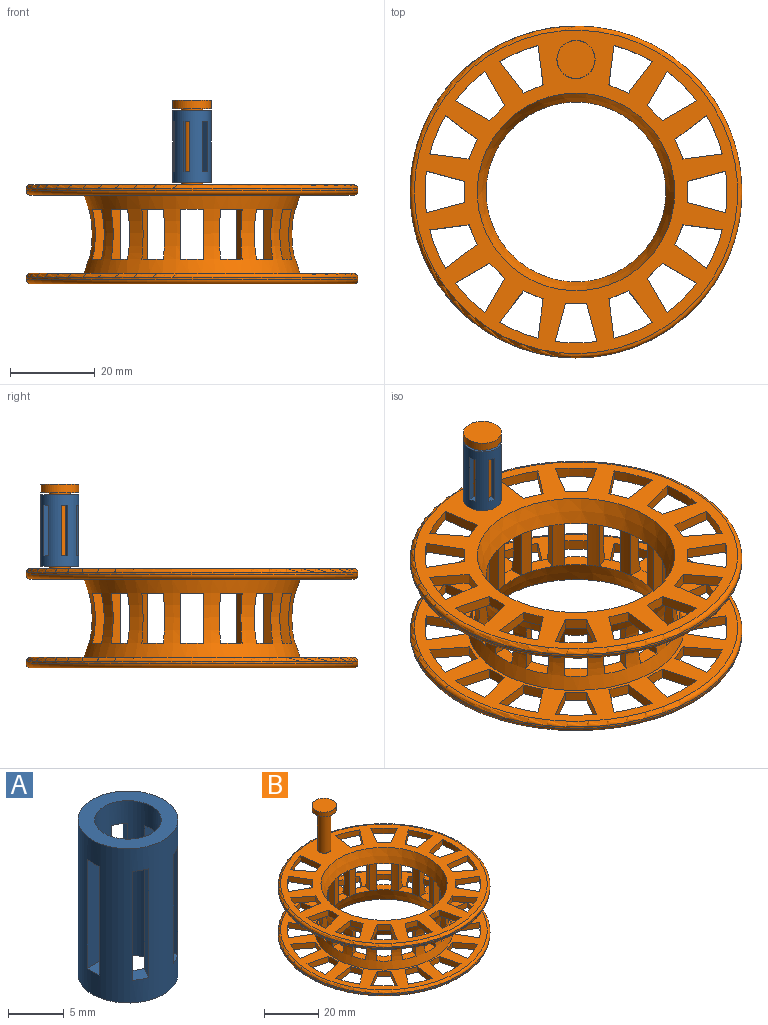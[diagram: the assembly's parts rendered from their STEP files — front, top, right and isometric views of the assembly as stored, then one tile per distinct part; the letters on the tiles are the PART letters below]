
ASSEMBLY  parts=2 mates=1
PART A: 28 faces, bbox 9x9x17 mm
  f0: cylinder r=4.5mm len=17mm, axis (0,0,1), area 372.2mm2, adj f2,f3,f4,f5,f6,f7,f8,f9
  f1: cylinder r=3mm len=17mm, axis (0,0,1), area 211.3mm2, adj f2,f3,f4,f5,f6,f7,f8,f9
  f2: plane 9x9mm, normal (0,0,1), area 35.3mm2, adj f0,f1
  f3: plane 9x9mm, normal (0,0,-1), area 35.3mm2, adj f0,f1
  f4: plane 12x1.33mm, normal (-0.87,0.5,0), area 18.4mm2, adj f0,f1,f6,f7
  f5: plane 12x1.33mm, normal (0.87,-0.5,0), area 18.4mm2, adj f0,f1,f6,f7
  f6: plane 2.08x2.07mm, normal (0,0,1), area 2.3mm2, adj f0,f1,f4,f5
  f7: plane 2.08x2.07mm, normal (0,0,-1), area 2.3mm2, adj f0,f1,f4,f5
  f8: plane 12x1.33mm, normal (-0.87,-0.5,0), area 18.4mm2, adj f0,f1,f10,f11
  f9: plane 12x1.33mm, normal (0.87,0.5,0), area 18.4mm2, adj f0,f1,f10,f11
  f10: plane 2.08x2.07mm, normal (0,0,1), area 2.3mm2, adj f0,f1,f8,f9
  f11: plane 2.08x2.07mm, normal (0,0,-1), area 2.3mm2, adj f0,f1,f8,f9
  f12: plane 12x1.53mm, normal (0,-1,0), area 18.4mm2, adj f0,f1,f14,f15
  f13: plane 12x1.53mm, normal (0,1,0), area 18.4mm2, adj f0,f1,f14,f15
  f14: plane 1.6x1.5mm, normal (0,0,1), area 2.3mm2, adj f0,f1,f12,f13
  f15: plane 1.6x1.5mm, normal (0,0,-1), area 2.3mm2, adj f0,f1,f12,f13
  f16: plane 12x1.33mm, normal (0.87,-0.5,0), area 18.4mm2, adj f0,f1,f18,f19
  f17: plane 12x1.33mm, normal (-0.87,0.5,0), area 18.4mm2, adj f0,f1,f18,f19
  f18: plane 2.08x2.07mm, normal (0,0,1), area 2.3mm2, adj f0,f1,f16,f17
  f19: plane 2.08x2.07mm, normal (0,0,-1), area 2.3mm2, adj f0,f1,f16,f17
  f20: plane 12x1.33mm, normal (0.87,0.5,0), area 18.4mm2, adj f0,f1,f22,f23
  f21: plane 12x1.33mm, normal (-0.87,-0.5,0), area 18.4mm2, adj f0,f1,f22,f23
  f22: plane 2.08x2.07mm, normal (0,0,1), area 2.3mm2, adj f0,f1,f20,f21
  f23: plane 2.08x2.07mm, normal (0,0,-1), area 2.3mm2, adj f0,f1,f20,f21
  f24: plane 12x1.53mm, normal (0,-1,0), area 18.4mm2, adj f0,f1,f25,f27
  f25: plane 1.6x1.5mm, normal (0,0,-1), area 2.3mm2, adj f0,f1,f24,f26
  f26: plane 12x1.53mm, normal (0,1,0), area 18.4mm2, adj f0,f1,f25,f27
  f27: plane 1.6x1.5mm, normal (0,0,1), area 2.3mm2, adj f0,f1,f24,f26
PART B: 221 faces, bbox 85x85x48.8 mm
  f0: cylinder r=21.25mm len=11.92mm, axis (0,0,1), area 33.7mm2, adj f20,f22,f203,f212
  f1: cylinder r=21.25mm len=11.92mm, axis (0,0,1), area 33.7mm2, adj f20,f22,f208,f211
  f2: cylinder r=21.25mm len=11.92mm, axis (0,0,1), area 33.7mm2, adj f20,f22,f151,f204
  f3: cylinder r=21.25mm len=11.92mm, axis (0,0,1), area 33.7mm2, adj f20,f22,f191,f200
  f4: cylinder r=21.25mm len=11.92mm, axis (0,0,1), area 33.7mm2, adj f20,f22,f196,f199
  f5: cylinder r=21.25mm len=11.92mm, axis (0,0,1), area 33.7mm2, adj f20,f22,f187,f192
  f6: cylinder r=21.25mm len=11.92mm, axis (0,0,1), area 33.7mm2, adj f20,f22,f188,f207
  f7: cylinder r=21.25mm len=11.92mm, axis (0,0,1), area 33.7mm2, adj f20,f22,f175,f184
  f8: cylinder r=21.25mm len=11.92mm, axis (0,0,1), area 33.7mm2, adj f20,f22,f180,f183
  f9: cylinder r=21.25mm len=11.92mm, axis (0,0,1), area 33.7mm2, adj f20,f22,f171,f176
  f10: cylinder r=21.25mm len=11.92mm, axis (0,0,1), area 33.7mm2, adj f20,f22,f172,f195
  f11: cylinder r=21.25mm len=11.92mm, axis (0,0,1), area 33.7mm2, adj f20,f22,f159,f168
  f12: cylinder r=21.25mm len=11.92mm, axis (0,0,1), area 33.7mm2, adj f20,f22,f164,f167
  f13: cylinder r=21.25mm len=11.92mm, axis (0,0,1), area 33.7mm2, adj f20,f22,f155,f160
  f14: cylinder r=21.25mm len=11.92mm, axis (0,0,1), area 33.7mm2, adj f20,f22,f156,f179
  f15: plane 76.5x76.5mm, normal (0,0,1), area 1821mm2, adj f20,f25,f26,f27,f28,f29,f30,f31
  f16: plane 76.5x76.5mm, normal (0,0,-1), area 1771.1mm2, adj f22,f85,f86,f87,f88,f89,f90,f91
  f17: plane 76.5x76.5mm, normal (0,0,1), area 1426.2mm2, adj f24,f85,f86,f87,f88,f89,f90,f91
  f18: plane 76.5x76.5mm, normal (0,0,-1), area 1495.7mm2, adj f24,f25,f26,f27,f28,f29,f30,f31
  f19: cylinder r=39.25mm len=78.5mm, axis (0,0,1), area 123.3mm2, adj f217,f220
  f20: cone r=23.36mm half-angle=20deg, axis (0,0,1), area 863.7mm2, adj f0,f1,f2,f3,f4,f5,f6,f7
  f21: cylinder r=21.25mm len=11.92mm, axis (0,0,1), area 33.7mm2, adj f20,f22,f152,f163
  f22: cone r=21.25mm half-angle=20deg, axis (0,0,-1), area 863.7mm2, adj f0,f1,f2,f3,f4,f5,f6,f7
  f23: cylinder r=39.25mm len=78.5mm, axis (0,0,1), area 123.3mm2, adj f218,f219
  f24: torus R=47.79mm, axis (0,0,1), area 1845.7mm2, adj f17,f18,f149,f150,f151,f152,f153,f154
  f25: plane 9.05x2.5mm, normal (-0.26,-0.97,0), area 23.4mm2, adj f15,f18,f26,f28
  f26: plane 5x2.5mm, normal (-1,0,0), area 12.5mm2, adj f15,f18,f25,f27
  f27: plane 9.05x2.5mm, normal (-0.26,0.97,0), area 23.4mm2, adj f15,f18,f26,f28
  f28: cylinder r=35.75mm len=9.85mm, axis (0,0,1), area 24.7mm2, adj f15,f18,f25,f27
  f29: plane 7.43x5.7mm, normal (-0.61,-0.79,0), area 23.4mm2, adj f15,f18,f30,f32
  f30: plane 4.62x2.5mm, normal (-0.92,0.38,0), area 12.5mm2, adj f15,f18,f29,f31
  f31: plane 9.29x2.5mm, normal (0.13,0.99,0), area 23.4mm2, adj f15,f18,f30,f32
  f32: cylinder r=35.75mm len=9.1mm, axis (0,0,1), area 24.7mm2, adj f15,f18,f29,f31
  f33: plane 9.29x2.5mm, normal (-0.99,-0.13,0), area 23.4mm2, adj f15,f18,f34,f36
  f34: plane 4.62x2.5mm, normal (-0.38,0.92,0), area 12.5mm2, adj f15,f18,f33,f35
  f35: plane 7.43x5.7mm, normal (0.79,0.61,0), area 23.4mm2, adj f15,f18,f34,f36
  f36: cylinder r=35.75mm len=9.1mm, axis (0,0,1), area 24.7mm2, adj f15,f18,f33,f35
  f37: plane 8.12x4.69mm, normal (-0.87,-0.5,0), area 23.4mm2, adj f15,f18,f38,f40
  f38: plane 3.54x3.54mm, normal (-0.71,0.71,0), area 12.5mm2, adj f15,f18,f37,f39
  f39: plane 8.12x4.69mm, normal (0.5,0.87,0), area 23.4mm2, adj f15,f18,f38,f40
  f40: cylinder r=35.75mm len=6.97mm, axis (0,0,1), area 24.7mm2, adj f15,f18,f37,f39
  f41: plane 9.05x2.5mm, normal (0.97,-0.26,0), area 23.4mm2, adj f15,f18,f42,f44
  f42: plane 5x2.5mm, normal (0,-1,0), area 12.5mm2, adj f15,f18,f41,f43
  f43: plane 9.05x2.5mm, normal (-0.97,-0.26,0), area 23.4mm2, adj f15,f18,f42,f44
  f44: cylinder r=35.75mm len=9.85mm, axis (0,0,1), area 24.7mm2, adj f15,f18,f41,f43
  f45: plane 7.43x5.7mm, normal (0.79,-0.61,0), area 23.4mm2, adj f15,f18,f46,f48
  f46: plane 4.62x2.5mm, normal (-0.38,-0.92,0), area 12.5mm2, adj f15,f18,f45,f47
  f47: plane 9.29x2.5mm, normal (-0.99,0.13,0), area 23.4mm2, adj f15,f18,f46,f48
  f48: cylinder r=35.75mm len=9.1mm, axis (0,0,1), area 24.7mm2, adj f15,f18,f45,f47
  f49: plane 9.29x2.5mm, normal (0.13,-0.99,0), area 23.4mm2, adj f15,f18,f50,f52
  f50: plane 4.62x2.5mm, normal (-0.92,-0.38,0), area 12.5mm2, adj f15,f18,f49,f51
  f51: plane 7.43x5.7mm, normal (-0.61,0.79,0), area 23.4mm2, adj f15,f18,f50,f52
  f52: cylinder r=35.75mm len=9.1mm, axis (0,0,1), area 24.7mm2, adj f15,f18,f49,f51
  f53: plane 8.12x4.69mm, normal (0.5,-0.87,0), area 23.4mm2, adj f15,f18,f54,f56
  f54: plane 3.54x3.54mm, normal (-0.71,-0.71,0), area 12.5mm2, adj f15,f18,f53,f55
  f55: plane 8.12x4.69mm, normal (-0.87,0.5,0), area 23.4mm2, adj f15,f18,f54,f56
  f56: cylinder r=35.75mm len=6.97mm, axis (0,0,1), area 24.7mm2, adj f15,f18,f53,f55
  f57: plane 9.05x2.5mm, normal (0.26,0.97,0), area 23.4mm2, adj f15,f18,f58,f60
  f58: plane 5x2.5mm, normal (1,0,0), area 12.5mm2, adj f15,f18,f57,f59
  f59: plane 9.05x2.5mm, normal (0.26,-0.97,0), area 23.4mm2, adj f15,f18,f58,f60
  f60: cylinder r=35.75mm len=9.85mm, axis (0,0,1), area 24.7mm2, adj f15,f18,f57,f59
  f61: plane 7.43x5.7mm, normal (0.61,0.79,0), area 23.4mm2, adj f15,f18,f62,f64
  f62: plane 4.62x2.5mm, normal (0.92,-0.38,0), area 12.5mm2, adj f15,f18,f61,f63
  f63: plane 9.29x2.5mm, normal (-0.13,-0.99,0), area 23.4mm2, adj f15,f18,f62,f64
  f64: cylinder r=35.75mm len=9.1mm, axis (0,0,1), area 24.7mm2, adj f15,f18,f61,f63
  f65: plane 9.29x2.5mm, normal (0.99,0.13,0), area 23.4mm2, adj f15,f18,f66,f68
  f66: plane 4.62x2.5mm, normal (0.38,-0.92,0), area 12.5mm2, adj f15,f18,f65,f67
  f67: plane 7.43x5.7mm, normal (-0.79,-0.61,0), area 23.4mm2, adj f15,f18,f66,f68
  f68: cylinder r=35.75mm len=9.1mm, axis (0,0,1), area 24.7mm2, adj f15,f18,f65,f67
  f69: plane 8.12x4.69mm, normal (0.87,0.5,0), area 23.4mm2, adj f15,f18,f70,f72
  f70: plane 3.54x3.54mm, normal (0.71,-0.71,0), area 12.5mm2, adj f15,f18,f69,f71
  f71: plane 8.12x4.69mm, normal (-0.5,-0.87,0), area 23.4mm2, adj f15,f18,f70,f72
  f72: cylinder r=35.75mm len=6.97mm, axis (0,0,1), area 24.7mm2, adj f15,f18,f69,f71
  f73: plane 7.43x5.7mm, normal (-0.79,0.61,0), area 23.4mm2, adj f15,f18,f74,f76
  f74: plane 4.62x2.5mm, normal (0.38,0.92,0), area 12.5mm2, adj f15,f18,f73,f75
  f75: plane 9.29x2.5mm, normal (0.99,-0.13,0), area 23.4mm2, adj f15,f18,f74,f76
  f76: cylinder r=35.75mm len=9.1mm, axis (0,0,1), area 24.7mm2, adj f15,f18,f73,f75
  f77: plane 9.29x2.5mm, normal (-0.13,0.99,0), area 23.4mm2, adj f15,f18,f78,f80
  f78: plane 4.62x2.5mm, normal (0.92,0.38,0), area 12.5mm2, adj f15,f18,f77,f79
  f79: plane 7.43x5.7mm, normal (0.61,-0.79,0), area 23.4mm2, adj f15,f18,f78,f80
  f80: cylinder r=35.75mm len=9.1mm, axis (0,0,1), area 24.7mm2, adj f15,f18,f77,f79
  f81: plane 8.12x4.69mm, normal (-0.5,0.87,0), area 23.4mm2, adj f15,f18,f82,f84
  f82: plane 3.54x3.54mm, normal (0.71,0.71,0), area 12.5mm2, adj f15,f18,f81,f83
  f83: plane 8.12x4.69mm, normal (0.87,-0.5,0), area 23.4mm2, adj f15,f18,f82,f84
  f84: cylinder r=35.75mm len=6.97mm, axis (0,0,1), area 24.7mm2, adj f15,f18,f81,f83
  f85: cylinder r=35.75mm len=9.85mm, axis (0,0,1), area 24.7mm2, adj f16,f17,f86,f88
  f86: plane 9.05x2.5mm, normal (0.97,0.26,0), area 23.4mm2, adj f16,f17,f85,f87
  f87: plane 5x2.5mm, normal (0,1,0), area 12.5mm2, adj f16,f17,f86,f88
  f88: plane 9.05x2.5mm, normal (-0.97,0.26,0), area 23.4mm2, adj f16,f17,f85,f87
  f89: cylinder r=35.75mm len=9.85mm, axis (0,0,1), area 24.7mm2, adj f16,f17,f90,f92
  f90: plane 9.05x2.5mm, normal (-0.26,0.97,0), area 23.4mm2, adj f16,f17,f89,f91
  f91: plane 5x2.5mm, normal (-1,0,0), area 12.5mm2, adj f16,f17,f90,f92
  f92: plane 9.05x2.5mm, normal (-0.26,-0.97,0), area 23.4mm2, adj f16,f17,f89,f91
  f93: cylinder r=35.75mm len=9.1mm, axis (0,0,1), area 24.7mm2, adj f16,f17,f94,f96
  f94: plane 9.29x2.5mm, normal (0.13,0.99,0), area 23.4mm2, adj f16,f17,f93,f95
  f95: plane 4.62x2.5mm, normal (-0.92,0.38,0), area 12.5mm2, adj f16,f17,f94,f96
  f96: plane 7.43x5.7mm, normal (-0.61,-0.79,0), area 23.4mm2, adj f16,f17,f93,f95
  f97: cylinder r=35.75mm len=9.1mm, axis (0,0,1), area 24.7mm2, adj f16,f17,f98,f100
  f98: plane 7.43x5.7mm, normal (0.79,0.61,0), area 23.4mm2, adj f16,f17,f97,f99
  f99: plane 4.62x2.5mm, normal (-0.38,0.92,0), area 12.5mm2, adj f16,f17,f98,f100
  f100: plane 9.29x2.5mm, normal (-0.99,-0.13,0), area 23.4mm2, adj f16,f17,f97,f99
  f101: cylinder r=35.75mm len=6.97mm, axis (0,0,1), area 24.7mm2, adj f16,f17,f102,f104
  f102: plane 8.12x4.69mm, normal (0.5,0.87,0), area 23.4mm2, adj f16,f17,f101,f103
  f103: plane 3.54x3.54mm, normal (-0.71,0.71,0), area 12.5mm2, adj f16,f17,f102,f104
  f104: plane 8.12x4.69mm, normal (-0.87,-0.5,0), area 23.4mm2, adj f16,f17,f101,f103
  f105: cylinder r=35.75mm len=9.85mm, axis (0,0,1), area 24.7mm2, adj f16,f17,f106,f108
  f106: plane 9.05x2.5mm, normal (-0.97,-0.26,0), area 23.4mm2, adj f16,f17,f105,f107
  f107: plane 5x2.5mm, normal (0,-1,0), area 12.5mm2, adj f16,f17,f106,f108
  f108: plane 9.05x2.5mm, normal (0.97,-0.26,0), area 23.4mm2, adj f16,f17,f105,f107
  f109: cylinder r=35.75mm len=9.1mm, axis (0,0,1), area 24.7mm2, adj f16,f17,f110,f112
  f110: plane 9.29x2.5mm, normal (-0.99,0.13,0), area 23.4mm2, adj f16,f17,f109,f111
  f111: plane 4.62x2.5mm, normal (-0.38,-0.92,0), area 12.5mm2, adj f16,f17,f110,f112
  f112: plane 7.43x5.7mm, normal (0.79,-0.61,0), area 23.4mm2, adj f16,f17,f109,f111
  f113: cylinder r=35.75mm len=9.1mm, axis (0,0,1), area 24.7mm2, adj f16,f17,f114,f116
  f114: plane 7.43x5.7mm, normal (-0.61,0.79,0), area 23.4mm2, adj f16,f17,f113,f115
  f115: plane 4.62x2.5mm, normal (-0.92,-0.38,0), area 12.5mm2, adj f16,f17,f114,f116
  f116: plane 9.29x2.5mm, normal (0.13,-0.99,0), area 23.4mm2, adj f16,f17,f113,f115
  f117: cylinder r=35.75mm len=6.97mm, axis (0,0,1), area 24.7mm2, adj f16,f17,f118,f120
  f118: plane 8.12x4.69mm, normal (-0.87,0.5,0), area 23.4mm2, adj f16,f17,f117,f119
  f119: plane 3.54x3.54mm, normal (-0.71,-0.71,0), area 12.5mm2, adj f16,f17,f118,f120
  f120: plane 8.12x4.69mm, normal (0.5,-0.87,0), area 23.4mm2, adj f16,f17,f117,f119
  f121: cylinder r=35.75mm len=9.85mm, axis (0,0,1), area 24.7mm2, adj f16,f17,f122,f124
  f122: plane 9.05x2.5mm, normal (0.26,-0.97,0), area 23.4mm2, adj f16,f17,f121,f123
  f123: plane 5x2.5mm, normal (1,0,0), area 12.5mm2, adj f16,f17,f122,f124
  f124: plane 9.05x2.5mm, normal (0.26,0.97,0), area 23.4mm2, adj f16,f17,f121,f123
  f125: cylinder r=35.75mm len=9.1mm, axis (0,0,1), area 24.7mm2, adj f16,f17,f126,f128
  f126: plane 9.29x2.5mm, normal (-0.13,-0.99,0), area 23.4mm2, adj f16,f17,f125,f127
  f127: plane 4.62x2.5mm, normal (0.92,-0.38,0), area 12.5mm2, adj f16,f17,f126,f128
  f128: plane 7.43x5.7mm, normal (0.61,0.79,0), area 23.4mm2, adj f16,f17,f125,f127
  f129: cylinder r=35.75mm len=9.1mm, axis (0,0,1), area 24.7mm2, adj f16,f17,f130,f132
  f130: plane 7.43x5.7mm, normal (-0.79,-0.61,0), area 23.4mm2, adj f16,f17,f129,f131
  f131: plane 4.62x2.5mm, normal (0.38,-0.92,0), area 12.5mm2, adj f16,f17,f130,f132
  f132: plane 9.29x2.5mm, normal (0.99,0.13,0), area 23.4mm2, adj f16,f17,f129,f131
  f133: cylinder r=35.75mm len=6.97mm, axis (0,0,1), area 24.7mm2, adj f16,f17,f134,f136
  f134: plane 8.12x4.69mm, normal (-0.5,-0.87,0), area 23.4mm2, adj f16,f17,f133,f135
  f135: plane 3.54x3.54mm, normal (0.71,-0.71,0), area 12.5mm2, adj f16,f17,f134,f136
  f136: plane 8.12x4.69mm, normal (0.87,0.5,0), area 23.4mm2, adj f16,f17,f133,f135
  f137: cylinder r=35.75mm len=9.1mm, axis (0,0,1), area 24.7mm2, adj f16,f17,f138,f140
  f138: plane 9.29x2.5mm, normal (0.99,-0.13,0), area 23.4mm2, adj f16,f17,f137,f139
  f139: plane 4.62x2.5mm, normal (0.38,0.92,0), area 12.5mm2, adj f16,f17,f138,f140
  f140: plane 7.43x5.7mm, normal (-0.79,0.61,0), area 23.4mm2, adj f16,f17,f137,f139
  f141: cylinder r=35.75mm len=9.1mm, axis (0,0,1), area 24.7mm2, adj f16,f17,f142,f144
  f142: plane 7.43x5.7mm, normal (0.61,-0.79,0), area 23.4mm2, adj f16,f17,f141,f143
  f143: plane 4.62x2.5mm, normal (0.92,0.38,0), area 12.5mm2, adj f16,f17,f142,f144
  f144: plane 9.29x2.5mm, normal (-0.13,0.99,0), area 23.4mm2, adj f16,f17,f141,f143
  f145: cylinder r=35.75mm len=6.97mm, axis (0,0,1), area 24.7mm2, adj f16,f17,f146,f148
  f146: plane 8.12x4.69mm, normal (0.87,-0.5,0), area 23.4mm2, adj f16,f17,f145,f147
  f147: plane 3.54x3.54mm, normal (0.71,0.71,0), area 12.5mm2, adj f16,f17,f146,f148
  f148: plane 8.12x4.69mm, normal (-0.5,0.87,0), area 23.4mm2, adj f16,f17,f145,f147
  f149: plane 5.5x3.43mm, normal (0,0,-1), area 17.9mm2, adj f20,f24,f151,f152
  f150: plane 5.5x3.43mm, normal (0,0,1), area 17.9mm2, adj f22,f24,f151,f152
  f151: plane 11.92x3.28mm, normal (-1,0,0), area 33mm2, adj f2,f24,f149,f150
  f152: plane 11.92x3.28mm, normal (1,0,0), area 33mm2, adj f21,f24,f149,f150
  f153: plane 5.5x3.43mm, normal (0,0,-1), area 17.9mm2, adj f20,f24,f155,f156
  f154: plane 5.5x3.43mm, normal (0,0,1), area 17.9mm2, adj f22,f24,f155,f156
  f155: plane 11.92x3.28mm, normal (0,-1,0), area 33mm2, adj f13,f24,f153,f154
  f156: plane 11.92x3.28mm, normal (0,1,0), area 33mm2, adj f14,f24,f153,f154
  f157: plane 6.33x5.13mm, normal (0,0,-1), area 17.9mm2, adj f20,f24,f159,f160
  f158: plane 6.33x5.13mm, normal (0,0,1), area 17.9mm2, adj f22,f24,f159,f160
  f159: plane 11.92x3.02mm, normal (-0.38,-0.92,0), area 33mm2, adj f11,f24,f157,f158
  f160: plane 11.92x3.02mm, normal (0.38,0.92,0), area 33mm2, adj f13,f24,f157,f158
  f161: plane 6.33x5.13mm, normal (0,0,-1), area 17.9mm2, adj f20,f24,f163,f164
  f162: plane 6.33x5.13mm, normal (0,0,1), area 17.9mm2, adj f22,f24,f163,f164
  f163: plane 11.92x3.02mm, normal (-0.92,-0.38,0), area 33mm2, adj f21,f24,f161,f162
  f164: plane 11.92x3.02mm, normal (0.92,0.38,0), area 33mm2, adj f12,f24,f161,f162
  f165: plane 6.2x6.2mm, normal (0,0,-1), area 17.9mm2, adj f20,f24,f167,f168
  f166: plane 6.2x6.2mm, normal (0,0,1), area 17.9mm2, adj f22,f24,f167,f168
  f167: plane 11.92x2.32mm, normal (-0.71,-0.71,0), area 33mm2, adj f12,f24,f165,f166
  f168: plane 11.92x2.32mm, normal (0.71,0.71,0), area 33mm2, adj f11,f24,f165,f166
  f169: plane 5.5x3.43mm, normal (0,0,-1), area 17.9mm2, adj f20,f24,f171,f172
  f170: plane 5.5x3.43mm, normal (0,0,1), area 17.9mm2, adj f22,f24,f171,f172
  f171: plane 11.92x3.28mm, normal (1,0,0), area 33mm2, adj f9,f24,f169,f170
  f172: plane 11.92x3.28mm, normal (-1,0,0), area 33mm2, adj f10,f24,f169,f170
  f173: plane 6.33x5.13mm, normal (0,0,-1), area 17.9mm2, adj f20,f24,f175,f176
  f174: plane 6.33x5.13mm, normal (0,0,1), area 17.9mm2, adj f22,f24,f175,f176
  f175: plane 11.92x3.02mm, normal (0.92,-0.38,0), area 33mm2, adj f7,f24,f173,f174
  f176: plane 11.92x3.02mm, normal (-0.92,0.38,0), area 33mm2, adj f9,f24,f173,f174
  f177: plane 6.33x5.13mm, normal (0,0,-1), area 17.9mm2, adj f20,f24,f179,f180
  f178: plane 6.33x5.13mm, normal (0,0,1), area 17.9mm2, adj f22,f24,f179,f180
  f179: plane 11.92x3.02mm, normal (0.38,-0.92,0), area 33mm2, adj f14,f24,f177,f178
  f180: plane 11.92x3.02mm, normal (-0.38,0.92,0), area 33mm2, adj f8,f24,f177,f178
  f181: plane 6.2x6.2mm, normal (0,0,-1), area 17.9mm2, adj f20,f24,f183,f184
  f182: plane 6.2x6.2mm, normal (0,0,1), area 17.9mm2, adj f22,f24,f183,f184
  f183: plane 11.92x2.32mm, normal (0.71,-0.71,0), area 33mm2, adj f8,f24,f181,f182
  f184: plane 11.92x2.32mm, normal (-0.71,0.71,0), area 33mm2, adj f7,f24,f181,f182
  f185: plane 5.5x3.43mm, normal (0,0,-1), area 17.9mm2, adj f20,f24,f187,f188
  f186: plane 5.5x3.43mm, normal (0,0,1), area 17.9mm2, adj f22,f24,f187,f188
  f187: plane 11.92x3.28mm, normal (0,1,0), area 33mm2, adj f5,f24,f185,f186
  f188: plane 11.92x3.28mm, normal (0,-1,0), area 33mm2, adj f6,f24,f185,f186
  f189: plane 6.33x5.13mm, normal (0,0,-1), area 17.9mm2, adj f20,f24,f191,f192
  f190: plane 6.33x5.13mm, normal (0,0,1), area 17.9mm2, adj f22,f24,f191,f192
  f191: plane 11.92x3.02mm, normal (0.38,0.92,0), area 33mm2, adj f3,f24,f189,f190
  f192: plane 11.92x3.02mm, normal (-0.38,-0.92,0), area 33mm2, adj f5,f24,f189,f190
  f193: plane 6.33x5.13mm, normal (0,0,-1), area 17.9mm2, adj f20,f24,f195,f196
  f194: plane 6.33x5.13mm, normal (0,0,1), area 17.9mm2, adj f22,f24,f195,f196
  f195: plane 11.92x3.02mm, normal (0.92,0.38,0), area 33mm2, adj f10,f24,f193,f194
  f196: plane 11.92x3.02mm, normal (-0.92,-0.38,0), area 33mm2, adj f4,f24,f193,f194
  f197: plane 6.2x6.2mm, normal (0,0,-1), area 17.9mm2, adj f20,f24,f199,f200
  f198: plane 6.2x6.2mm, normal (0,0,1), area 17.9mm2, adj f22,f24,f199,f200
  f199: plane 11.92x2.32mm, normal (0.71,0.71,0), area 33mm2, adj f4,f24,f197,f198
  f200: plane 11.92x2.32mm, normal (-0.71,-0.71,0), area 33mm2, adj f3,f24,f197,f198
  f201: plane 6.33x5.13mm, normal (0,0,-1), area 17.9mm2, adj f20,f24,f203,f204
  f202: plane 6.33x5.13mm, normal (0,0,1), area 17.9mm2, adj f22,f24,f203,f204
  f203: plane 11.92x3.02mm, normal (-0.92,0.38,0), area 33mm2, adj f0,f24,f201,f202
  f204: plane 11.92x3.02mm, normal (0.92,-0.38,0), area 33mm2, adj f2,f24,f201,f202
  f205: plane 6.33x5.13mm, normal (0,0,-1), area 17.9mm2, adj f20,f24,f207,f208
  f206: plane 6.33x5.13mm, normal (0,0,1), area 17.9mm2, adj f22,f24,f207,f208
  f207: plane 11.92x3.02mm, normal (-0.38,0.92,0), area 33mm2, adj f6,f24,f205,f206
  f208: plane 11.92x3.02mm, normal (0.38,-0.92,0), area 33mm2, adj f1,f24,f205,f206
  f209: plane 6.2x6.2mm, normal (0,0,-1), area 17.9mm2, adj f20,f24,f211,f212
  f210: plane 6.2x6.2mm, normal (0,0,1), area 17.9mm2, adj f22,f24,f211,f212
  f211: plane 11.92x2.32mm, normal (-0.71,0.71,0), area 33mm2, adj f1,f24,f209,f210
  f212: plane 11.92x2.32mm, normal (0.71,-0.71,0), area 33mm2, adj f0,f24,f209,f210
  f213: cylinder r=2.5mm len=18mm, axis (0,0,1), area 282.7mm2, adj f15,f216
  f214: plane 9x9mm, normal (0,0,1), area 63.6mm2, adj f215
  f215: cylinder r=4.5mm len=9mm, axis (0,0,1), area 56.5mm2, adj f214,f216
  f216: plane 9x9mm, normal (0,0,-1), area 44mm2, adj f213,f215
  f217: torus R=38.25mm, axis (0,0,-1), area 383.8mm2, adj f15,f19
  f218: torus R=38.25mm, axis (0,0,1), area 383.8mm2, adj f16,f23
  f219: torus R=38.25mm, axis (0,0,-1), area 383.8mm2, adj f17,f23
  f220: torus R=38.25mm, axis (0,0,1), area 383.8mm2, adj f18,f19
PLACE A rot(axis=(-0.99,-0.12,0),180deg) t=(2.76,53.51,49.33)mm
PLACE B t=(10.13,-8.21,6.83)mm fixed
MATE revolute A.f0 <-> B.f213  axis (0,0,1) through (10.13,23.09,19.08)mm
